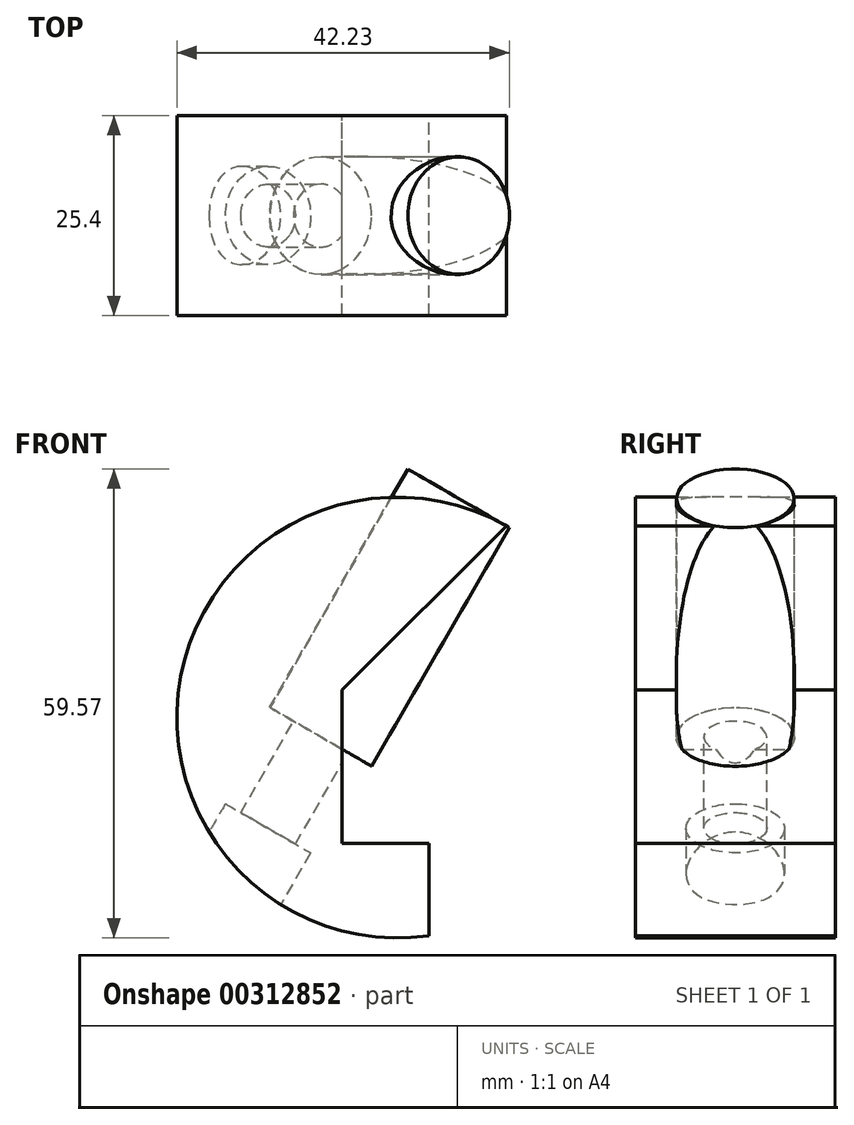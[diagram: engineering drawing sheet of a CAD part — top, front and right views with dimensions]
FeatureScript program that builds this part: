
annotation { "Feature Type Name" : "Feature", "Feature Type Description" : "" }
export const myFeature = defineFeature(function(context is Context, id is Id, definition is map)
    precondition{}
    {
        {
            var Q0;
            Q0=qCreatedBy(makeId("Front.planeOp"),FACE);
            var sketch = newSketch(context, id + "F0", { "sketchPlane" : qUnion([Q0])});
            skArc(sketch, "E0", {"start": v(13.84, 24.34) * mm, "mid": v(-27.51, 5.2) * mm, "end": v(4, -27.71) * mm});
            skLineSegment(sketch, "E1", {"start": v(-38.1, -28) * mm, "end": v(40.65, -28) * mm, "construction": true});
            skLineSegment(sketch, "E2", {"start": v(-28, 26.5) * mm, "end": v(-28, -21.8) * mm, "construction": true});
            skLineSegment(sketch, "E3", {"start": v(-7, 3.5) * mm, "end": v(-7, -16) * mm});
            skLineSegment(sketch, "E4", {"start": v(-7, -16) * mm, "end": v(4, -16) * mm});
            skLineSegment(sketch, "E5", {"start": v(-7, 3.5) * mm, "end": v(13.84, 24.34) * mm});
            skLineSegment(sketch, "E6", {"start": v(4, -16) * mm, "end": v(4, -27.71) * mm});
            skArc(sketch, "E7", {"start": v(4, -27.71) * mm, "mid": v(27.51, -5.2) * mm, "end": v(13.84, 24.34) * mm, "construction": true});
            skSolve(sketch);
        }
        {
            var Q0;
            Q0 = qSketchRegion(id + "F0", true);
            extrude(context, id + "F1", {"entities" : qUnion([Q0]), "endBound" : BoundingType.SYMMETRIC, "depth" : 25.4 * mm});
        }
        {
            var Q0;
            Q0=makeQuery(id+"F1.opExtrude","SWEPT_EDGE",EDGE,{"disambiguationData":[OSD([sQuery(id+"F0.wireOp",EDGE,"E0"),sQuery(id+"F0.wireOp",EDGE,"E5")])]});
            cPlane(context, id + "F2", {"entities" : qUnion([Q0]), "cplaneType" : CPlaneType.LINE_ANGLE, "offset" : 25 * mm, "angle" : 150 * degree, "oppositeDirection" : true, "width" : 150 * mm, "height" : 150 * mm});
        }
        {
            var Q0;
            Q0=qCreatedBy(id+"F2.planeOp",FACE);
            var sketch = newSketch(context, id + "F3", { "sketchPlane" : qUnion([Q0])});
            skCircle(sketch, "E8", {"center": v(-7.18, 0) * mm, "radius": 7.5 * mm});
            skSolve(sketch);
        }
        {
            var Q0;
            Q0=makeQuery(id+"F3.imprint","IMPRINT",FACE,{"disambiguationData":[TD([[makeQuery(id+"F3.imprint","IMPRINT",EDGE,{"derivedFrom":sQuery(id+"F3.wireOp",EDGE,"E8")}),1.0]])]});
            extrude(context, id + "F4", {"entities" : qUnion([Q0]), "operationType" : NewBodyOperationType.REMOVE, "depth" : 35 * mm});
        }
        {
            var Q0;
            Q0=makeQuery(id+"F4.boolean.opBoolean","COPY",FACE,{"derivedFrom":makeQuery(id+"F4.opExtrude","CAP_FACE",FACE,{"disambiguationData":[OSD([sQuery(id+"F3.wireOp",EDGE,"E8")])],"isStart":false})});
            var sketch = newSketch(context, id + "F5", { "sketchPlane" : qUnion([Q0])});
            skCircle(sketch, "E9", {"center": v(-7.18, 0) * mm, "radius": 4 * mm});
            skSolve(sketch);
        }
        {
            var Q0;
            Q0=makeQuery(id+"F5.imprint","IMPRINT",FACE,{"disambiguationData":[TD([[makeQuery(id+"F5.imprint","IMPRINT",EDGE,{"derivedFrom":sQuery(id+"F5.wireOp",EDGE,"E9")}),1.0]])]});
            extrude(context, id + "F6", {"entities" : qUnion([Q0]), "operationType" : NewBodyOperationType.REMOVE, "oppositeDirection" : true, "depth" : 25 * mm});
        }
        {
            var Q0;
            Q0=qCreatedBy(id+"F2.planeOp",FACE);
            cPlane(context, id + "F7", {"entities" : qUnion([Q0]), "cplaneType" : CPlaneType.OFFSET, "offset" : 56.4 * mm, "width" : 150 * mm, "height" : 150 * mm});
        }
        {
            var Q0;
            Q0=qCreatedBy(id+"F7.planeOp",FACE);
            var sketch = newSketch(context, id + "F8", { "sketchPlane" : qUnion([Q0])});
            skCircle(sketch, "E10", {"center": v(-7.18, 0) * mm, "radius": 6.25 * mm});
            skSolve(sketch);
        }
        {
            var Q0;
            Q0=makeQuery(id+"F8.imprint","IMPRINT",FACE,{"disambiguationData":[TD([[makeQuery(id+"F8.imprint","IMPRINT",EDGE,{"derivedFrom":sQuery(id+"F8.wireOp",EDGE,"E10")}),1.0]])]});
            extrude(context, id + "F9", {"entities" : qUnion([Q0]), "operationType" : NewBodyOperationType.REMOVE, "oppositeDirection" : true, "depth" : 8 * mm});
        }
        {
            var Q0;
            Q0=makeQuery(id+"F4.boolean.opBoolean","COPY",FACE,{"derivedFrom":makeQuery(id+"F4.opExtrude","CAP_FACE",FACE,{"disambiguationData":[OSD([sQuery(id+"F3.wireOp",EDGE,"E8")])],"isStart":false})});
            var sketch = newSketch(context, id + "F10", { "sketchPlane" : qUnion([Q0])});
            skCircle(sketch, "E11", {"center": v(-7.18, 0) * mm, "radius": 7.45 * mm});
            skSolve(sketch);
        }
        {
            var Q0;
            Q0 = qSketchRegion(id + "F10", true);
            extrude(context, id + "F11", {"entities" : qUnion([Q0]), "depth" : 35 * mm});
        }
    });
